# Revit family: Tiefen_und_Plattener_Staberder_OMEX
name_source: partatom
category: Generic Models
revit_build: Autodesk Revit 2015 (Build: 20140606_1530(x64)
units: mm (PartAtom-declared; Revit-internal decimal feet)

## types (3) — shared parameters
Lenght 2 = 44 mm  [stored 0.144357 ft]
Manufacturer = OBO Bettermann
Material = Steel, Galvanized
URL = http://www.obo-bettermann.com

## per-type parameters (varying)
| type | Article Type | Diameter dimesion | GTIN | Manufacturer Art. No. | Outer Diameter Dimension |
| 219 25 OMEX FT | 219 25 OMEX FT | 13 mm | 4012195371359 | 50000025 | 7 mm  [stored 0.0229659 ft] |
| 219 20 OMEX FT(2) | 219 20 OMEX FT | 10 mm  [stored 0.0328084 ft] | 4012195371472 | 50000203 | 6 mm  [stored 0.019685 ft] |
| 219 20 OMEX FT | 219 20 OMEX FT | 10 mm  [stored 0.0328084 ft] | 4012195371298 | 50000017 | 6 mm  [stored 0.019685 ft] |

note: [stored X ft] marks values corroborated as IEEE doubles in the binary element streams (Revit-internal decimal feet)

## geometry (parser evidence)
native form markers: Sweep x2
no freeform markers — native parametric forms only
